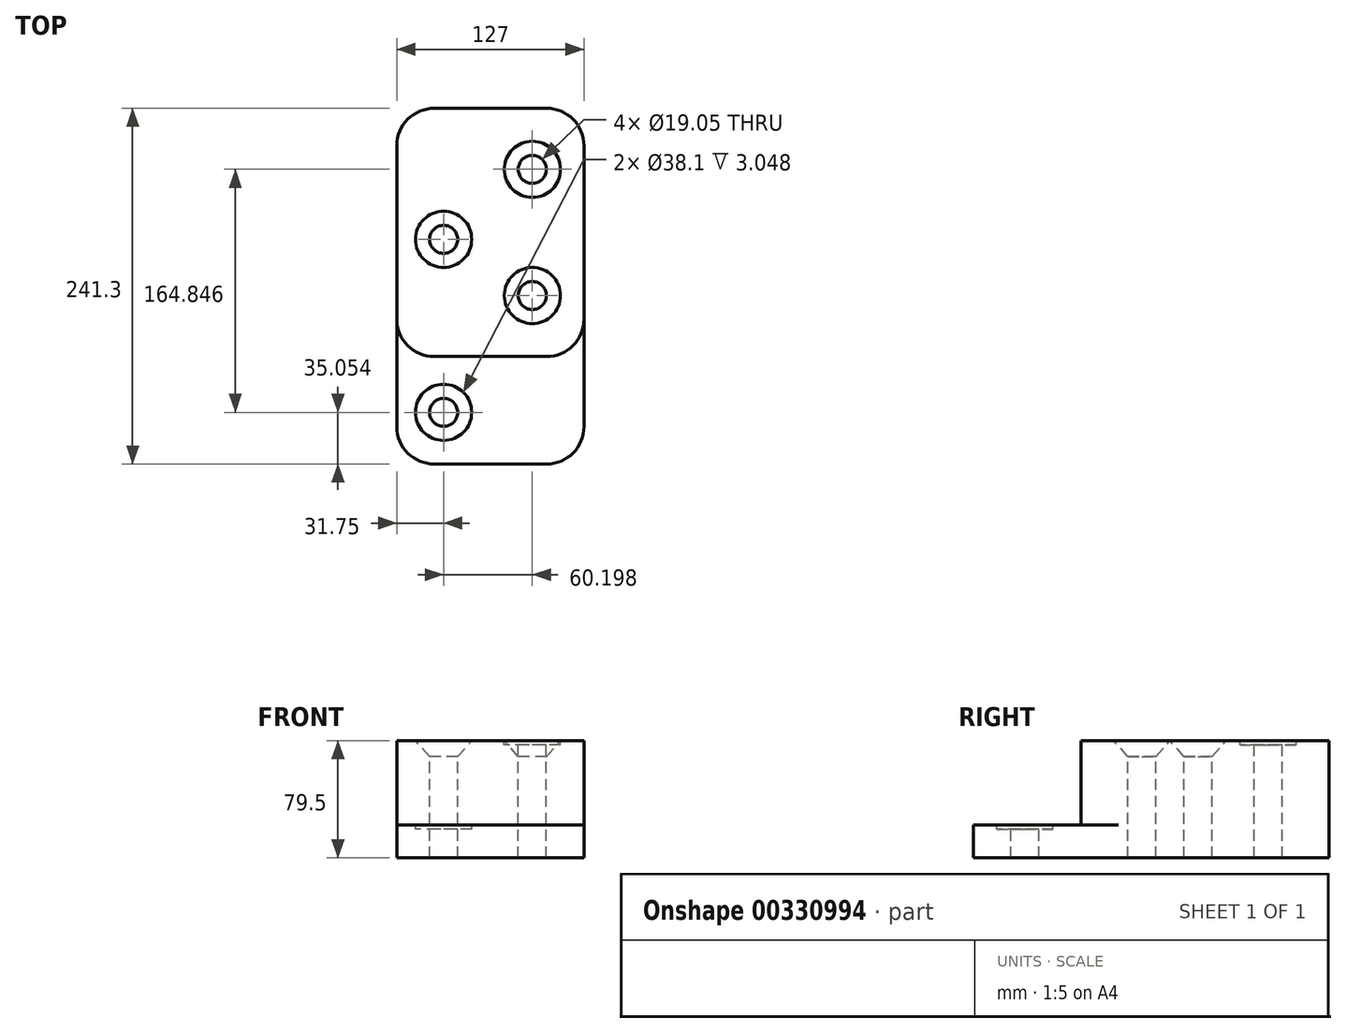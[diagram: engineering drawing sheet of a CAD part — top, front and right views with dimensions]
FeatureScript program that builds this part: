
annotation { "Feature Type Name" : "Feature", "Feature Type Description" : "" }
export const myFeature = defineFeature(function(context is Context, id is Id, definition is map)
    precondition{}
    {
        {
            var Q0;
            Q0=qCreatedBy(makeId("Top.planeOp"),FACE);
            var sketch = newSketch(context, id + "F0", { "sketchPlane" : qUnion([Q0])});
            skLineSegment(sketch, "E0", {"start": v(0, 25.4) * mm, "end": v(0, 143) * mm});
            skLineSegment(sketch, "E1", {"start": v(25.4, 168.4) * mm, "end": v(101.6, 168.4) * mm});
            skLineSegment(sketch, "E2", {"start": v(127, 143) * mm, "end": v(127, 25.4) * mm});
            skLineSegment(sketch, "E3", {"start": v(101.6, 0) * mm, "end": v(25.4, 0) * mm});
            skPoint(sketch, "E4.visualSharp", {"position": v(0, 168.4) * mm});
            skArc(sketch, "E4.filletArc", {"start": v(25.4, 168.4) * mm, "mid": v(7.44, 160.96) * mm, "end": v(0, 143) * mm});
            skPoint(sketch, "E5.visualSharp", {"position": v(0, 0) * mm});
            skArc(sketch, "E5.filletArc", {"start": v(0, 25.4) * mm, "mid": v(7.44, 7.44) * mm, "end": v(25.4, 0) * mm});
            skPoint(sketch, "E6.visualSharp", {"position": v(127, 168.4) * mm});
            skArc(sketch, "E6.filletArc", {"start": v(127, 143) * mm, "mid": v(119.56, 160.96) * mm, "end": v(101.6, 168.4) * mm});
            skPoint(sketch, "E7.visualSharp", {"position": v(127, 0) * mm});
            skArc(sketch, "E7.filletArc", {"start": v(101.6, 0) * mm, "mid": v(119.56, 7.44) * mm, "end": v(127, 25.4) * mm});
            skPoint(sketch, "E8", {"position": v(31.75, 79.5) * mm});
            skPoint(sketch, "E9", {"position": v(91.95, 127) * mm});
            skPoint(sketch, "E10", {"position": v(91.95, 41.4) * mm});
            skLineSegment(sketch, "E11", {"start": v(0, 25.4) * mm, "end": v(0, -47.5) * mm});
            skLineSegment(sketch, "E12", {"start": v(25.4, -72.9) * mm, "end": v(101.6, -72.9) * mm});
            skLineSegment(sketch, "E13", {"start": v(127, -47.5) * mm, "end": v(127, 25.4) * mm});
            skPoint(sketch, "E14.visualSharp", {"position": v(0, -72.9) * mm});
            skArc(sketch, "E14.filletArc", {"start": v(0, -47.5) * mm, "mid": v(7.44, -65.46) * mm, "end": v(25.4, -72.9) * mm});
            skPoint(sketch, "E15.visualSharp", {"position": v(127, -72.9) * mm});
            skArc(sketch, "E15.filletArc", {"start": v(101.6, -72.9) * mm, "mid": v(119.56, -65.46) * mm, "end": v(127, -47.5) * mm});
            skPoint(sketch, "E16", {"position": v(31.75, -37.85) * mm});
            skSolve(sketch);
        }
        {
            var Q0;
            Q0=makeQuery(id+"F0.imprint","IMPRINT",FACE,{"disambiguationData":[TD([[makeQuery(id+"F0.imprint","IMPRINT",EDGE,{"derivedFrom":sQuery(id+"F0.wireOp",EDGE,"E3")}),1.0]])]});
            extrude(context, id + "F1", {"entities" : qUnion([Q0]), "depth" : 22.35 * mm});
        }
        {
            var Q0;
            Q0=makeQuery(id+"F0.imprint","IMPRINT",FACE,{"disambiguationData":[TD([[makeQuery(id+"F0.imprint","IMPRINT",EDGE,{"derivedFrom":sQuery(id+"F0.wireOp",EDGE,"E0")}),-1.0]])]});
            extrude(context, id + "F2", {"entities" : qUnion([Q0]), "operationType" : NewBodyOperationType.ADD, "depth" : 79.5 * mm});
        }
        {
            var Q0;
            Q0=makeQuery(id+"F2.opExtrude","CAP_FACE",FACE,{"disambiguationData":[OSD([sQuery(id+"F0.wireOp",EDGE,"E0"),sQuery(id+"F0.wireOp",EDGE,"E1"),sQuery(id+"F0.wireOp",EDGE,"E2"),sQuery(id+"F0.wireOp",EDGE,"E3"),sQuery(id+"F0.wireOp",EDGE,"E4.filletArc"),sQuery(id+"F0.wireOp",EDGE,"E5.filletArc"),sQuery(id+"F0.wireOp",EDGE,"E6.filletArc"),sQuery(id+"F0.wireOp",EDGE,"E7.filletArc")])],"isStart":false});
            var sketch = newSketch(context, id + "F3", { "sketchPlane" : qUnion([Q0])});
            skPoint(sketch, "E17", {"position": v(91.95, 127) * mm});
            skPoint(sketch, "E18", {"position": v(31.75, 79.5) * mm});
            skPoint(sketch, "E19", {"position": v(91.95, 41.4) * mm});
            skSolve(sketch);
        }
        {
            var Q0;
            Q0=makeQuery(id+"F1.opExtrude","CAP_FACE",FACE,{"disambiguationData":[OSD([sQuery(id+"F0.wireOp",EDGE,"E3"),sQuery(id+"F0.wireOp",EDGE,"E5.filletArc"),sQuery(id+"F0.wireOp",EDGE,"E7.filletArc"),sQuery(id+"F0.wireOp",EDGE,"E11"),sQuery(id+"F0.wireOp",EDGE,"E12"),sQuery(id+"F0.wireOp",EDGE,"E13"),sQuery(id+"F0.wireOp",EDGE,"E14.filletArc"),sQuery(id+"F0.wireOp",EDGE,"E15.filletArc")])],"isStart":false});
            var sketch = newSketch(context, id + "F4", { "sketchPlane" : qUnion([Q0])});
            skPoint(sketch, "E20", {"position": v(31.75, -37.85) * mm});
            skSolve(sketch);
        }
        {
            var Q0;
            Q0=sQuery(id+"F3.wireOp",VERTEX,"E17");
            var Q1;
            Q1=sQuery(id+"F4.wireOp",VERTEX,"E20");
            var Q2;
            Q2=makeQuery(id+"F1.opExtrude","SWEPT_BODY",BODY,{"disambiguationData":[OSD([sQuery(id+"F0.wireOp",EDGE,"E3"),sQuery(id+"F0.wireOp",EDGE,"E5.filletArc"),sQuery(id+"F0.wireOp",EDGE,"E7.filletArc"),sQuery(id+"F0.wireOp",EDGE,"E11"),sQuery(id+"F0.wireOp",EDGE,"E12"),sQuery(id+"F0.wireOp",EDGE,"E13"),sQuery(id+"F0.wireOp",EDGE,"E14.filletArc"),sQuery(id+"F0.wireOp",EDGE,"E15.filletArc")])]});
            hole(context, id + "F5", {"style" : HoleStyle.C_BORE, "endStyle" : HoleEndStyle.THROUGH, "holeDiameter" : 19.05 * mm, "cBoreDiameter" : 38.1 * mm, "cBoreDepth" : 3.05 * mm, "tappedDepth" : 12.7 * mm, "tapClearance" : 3, "locations" : qUnion([Q0, Q1]), "scope" : qUnion([Q2])});
        }
        {
            var Q0;
            Q0=sQuery(id+"F3.wireOp",VERTEX,"E18");
            var Q1;
            Q1=sQuery(id+"F3.wireOp",VERTEX,"E19");
            var Q2;
            Q2=makeQuery(id+"F1.opExtrude","SWEPT_BODY",BODY,{"disambiguationData":[OSD([sQuery(id+"F0.wireOp",EDGE,"E3"),sQuery(id+"F0.wireOp",EDGE,"E5.filletArc"),sQuery(id+"F0.wireOp",EDGE,"E7.filletArc"),sQuery(id+"F0.wireOp",EDGE,"E11"),sQuery(id+"F0.wireOp",EDGE,"E12"),sQuery(id+"F0.wireOp",EDGE,"E13"),sQuery(id+"F0.wireOp",EDGE,"E14.filletArc"),sQuery(id+"F0.wireOp",EDGE,"E15.filletArc")])]});
            hole(context, id + "F6", {"style" : HoleStyle.C_SINK, "endStyle" : HoleEndStyle.THROUGH, "holeDiameter" : 19.05 * mm, "cSinkDiameter" : 38.1 * mm, "cSinkAngle" : 82 * degree, "tappedDepth" : 12.7 * mm, "tapClearance" : 3, "locations" : qUnion([Q0, Q1]), "scope" : qUnion([Q2])});
        }
    });
